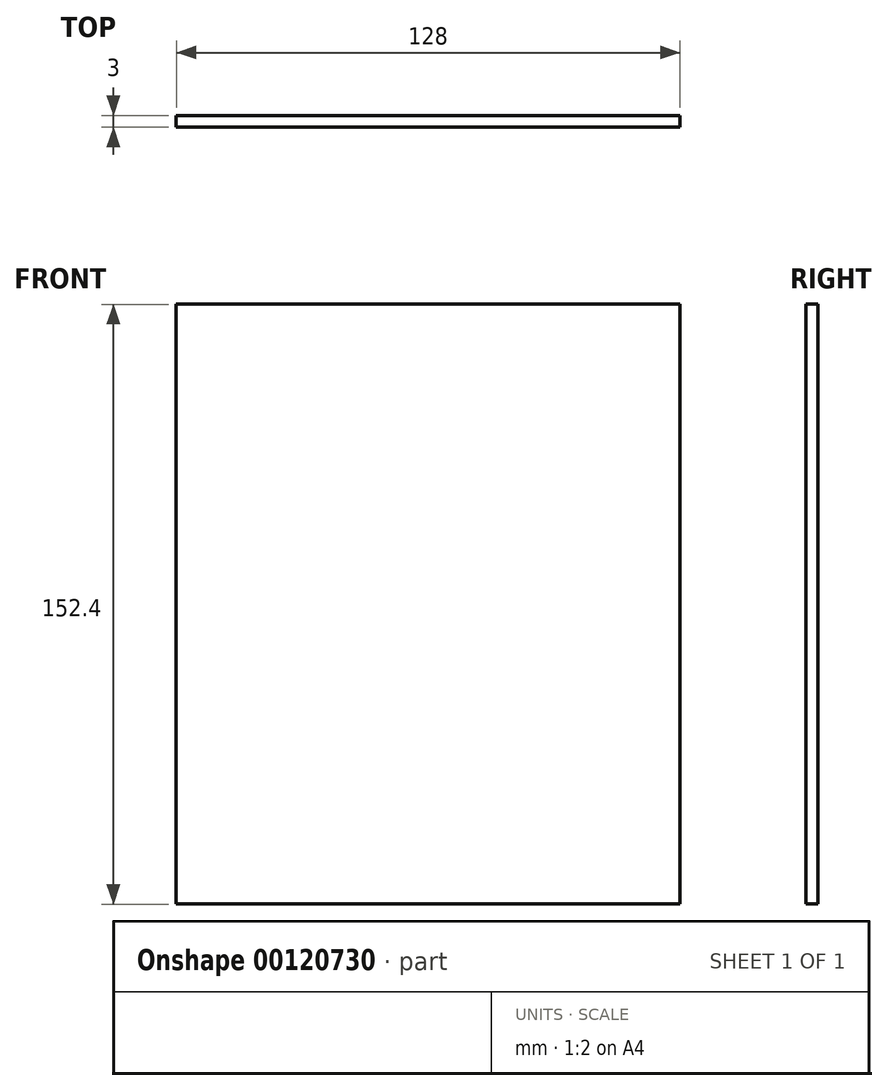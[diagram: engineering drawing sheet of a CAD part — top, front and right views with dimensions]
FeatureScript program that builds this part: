
annotation { "Feature Type Name" : "Feature", "Feature Type Description" : "" }
export const myFeature = defineFeature(function(context is Context, id is Id, definition is map)
    precondition{}
    {
        {
            var Q0;
            Q0=qCreatedBy(makeId("Front.planeOp"),FACE);
            var sketch = newSketch(context, id + "F0", { "sketchPlane" : qUnion([Q0])});
            skLineSegment(sketch, "E0.bottom", {"start": v(-64.45, 96.74) * mm, "end": v(63.55, 96.74) * mm});
            skLineSegment(sketch, "E0.top", {"start": v(-64.45, -55.66) * mm, "end": v(63.55, -55.66) * mm});
            skLineSegment(sketch, "E0.left", {"start": v(-64.45, 96.74) * mm, "end": v(-64.45, -55.66) * mm});
            skLineSegment(sketch, "E0.right", {"start": v(63.55, 96.74) * mm, "end": v(63.55, -55.66) * mm});
            skSolve(sketch);
        }
        {
            var Q0;
            Q0=qSketchRegion(id+"F0",true);
            extrude(context, id + "F1", {"entities" : qUnion([Q0]), "depth" : 3 * mm});
        }
    });
